# Revit family: Control_Unit-Lutron-Ethernet_Control_Interface
name_source: partatom
category: Lighting Devices
revit_build: Autodesk Revit 2017 (Build: 20160720_1515(x64)
units: mm (PartAtom-declared; Revit-internal decimal feet)

## family parameters
Cut with Voids When Loaded = No
Host = Face
Maintain Annotation Orientation = Yes
OmniClass Number = 23.85.80.11
OmniClass Title = Building Controls
Part Type = Normal
Room Calculation Point = No
Round Connector Dimension = Use Radius
Shared = No

## types (1)
- QSE-CI-NWK-E
    Apparent Power = 2 VA
    Assembly Code = D5020200
    Chamfer Edge = 0' - 0 1/16"
    Controller Material = Plastic - Lutron - Black
    Cost = 0 $
    Current = 0 A
    Default Elevation = 4' - 0"
    Description = QSE-CI-NWK-E Control Interface
    Instruction Sheet Link = http://www.lutron.com
    Label = NWK
    Load Classification = Other
    Manufacturer = Lutron Electronics Co., Inc
    Manufacturer Fax Number = 610-282-1243
    Maximum Operating Temperature = 104 °F
    Minimum Operating Temperature = 32 °F
    Model = QSE-CI-NWK-E
    Mount Center Curve Diameter = 0' - 0 1/2"
    Mount Center Curve Radius = 0' - 0 1/4"
    Mount Cutout Depth = 0' - 0 25/32"
    Mount Edge Curve Diameter = 0' - 0 1/4"
    Mount Edge Curve Radius = 0' - 0 1/8"
    Mount Reveal Width Center Offset = 0' - 3 1/4"
    Mounting Reveal Depth = 0' - 0 9/32"
    Mounting Reveal Height = 0' - 0 3/4"
    Number of Poles = 1
    Operating Voltage = 24 V - 36 V
    Overall Depth = 0' - 1"
    Overall Height = 0' - 4 1/4"
    Overall Width = 0' - 5 1/4"
    Performance URL = http://www.lutron.com
    Product Documentation Link = http://www.lutron.com
    Product Name = QSE-CI-NWK-E Control Interface
    Product Page URL = http://www.lutron.com
    Series = QS
    URL = http://www.lutron.com
    Version = 2017 - v1.0b
    Video Link = https://www.youtube.com
    Voltage = 36 V
    Warranty URL = http://www.lutron.com

## geometry (parser evidence)
native form markers: Sweep x3
no freeform markers — native parametric forms only
